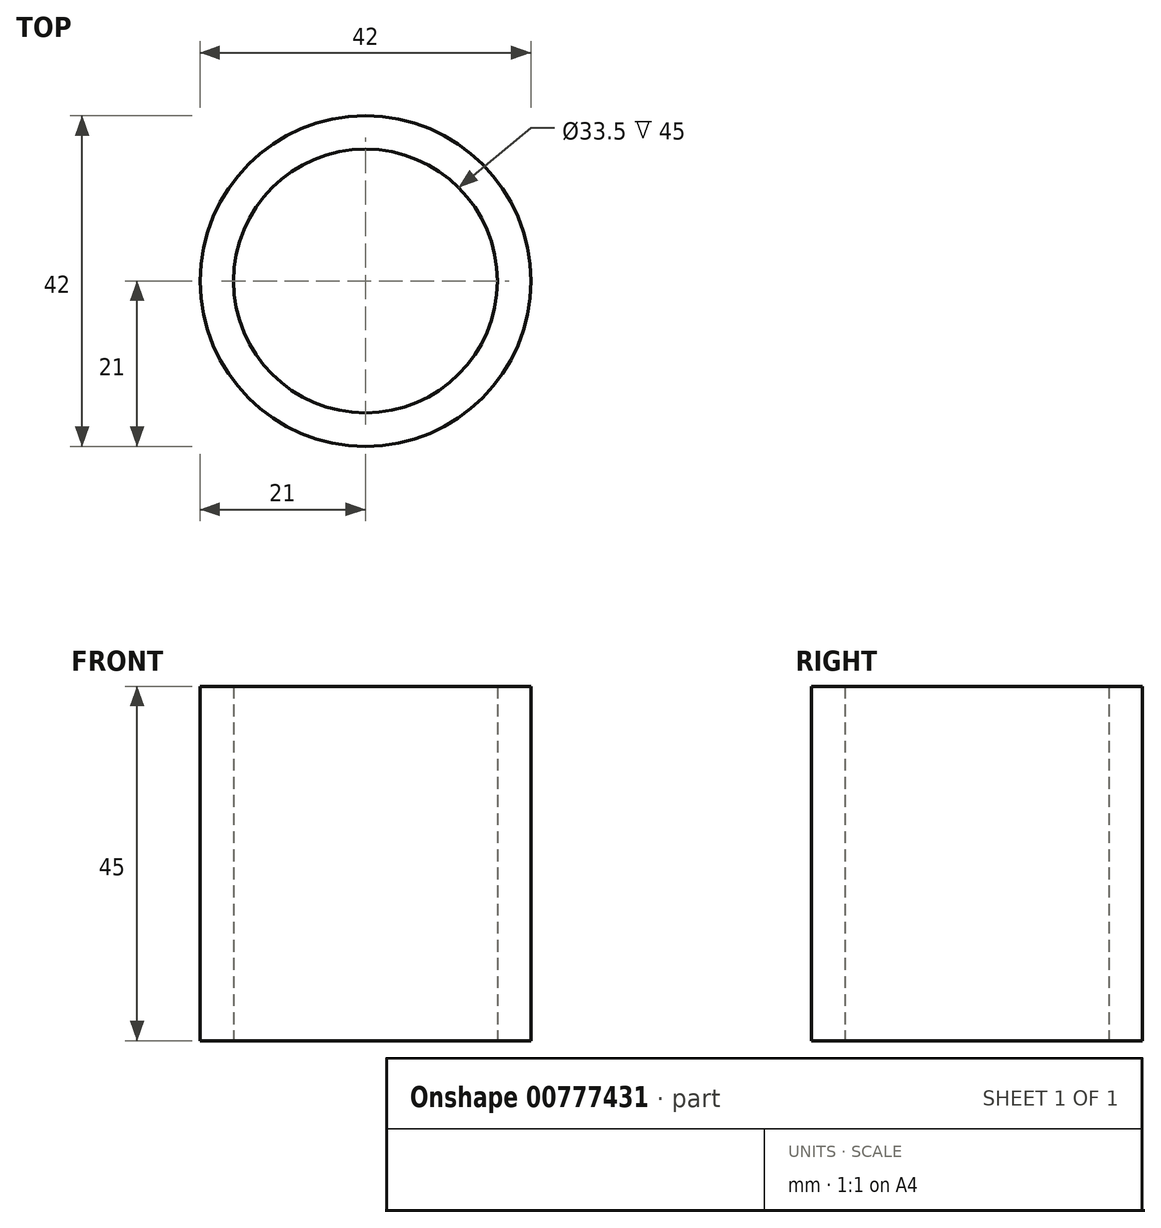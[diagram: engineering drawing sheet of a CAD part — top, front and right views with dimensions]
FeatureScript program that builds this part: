
annotation { "Feature Type Name" : "Feature", "Feature Type Description" : "" }
export const myFeature = defineFeature(function(context is Context, id is Id, definition is map)
    precondition{}
    {
        {
            var Q0;
            Q0=qCreatedBy(makeId("Top.planeOp"),FACE);
            var sketch = newSketch(context, id + "F0", { "sketchPlane" : qUnion([Q0])});
            skCircle(sketch, "E0", {"center": v(0, 0) * mm, "radius": 16.75 * mm});
            skCircle(sketch, "E1", {"center": v(0, 0) * mm, "radius": 21 * mm});
            skSolve(sketch);
        }
        {
            var Q0;
            Q0=makeQuery(id+"F0.imprint","IMPRINT",FACE,{"disambiguationData":[TD([[makeQuery(id+"F0.imprint","IMPRINT",EDGE,{"derivedFrom":sQuery(id+"F0.wireOp",EDGE,"E0")}),-1.0]])]});
            extrude(context, id + "F1", {"entities" : qUnion([Q0]), "depth" : 45 * mm, "offsetDistance" : 25 * mm});
        }
    });
